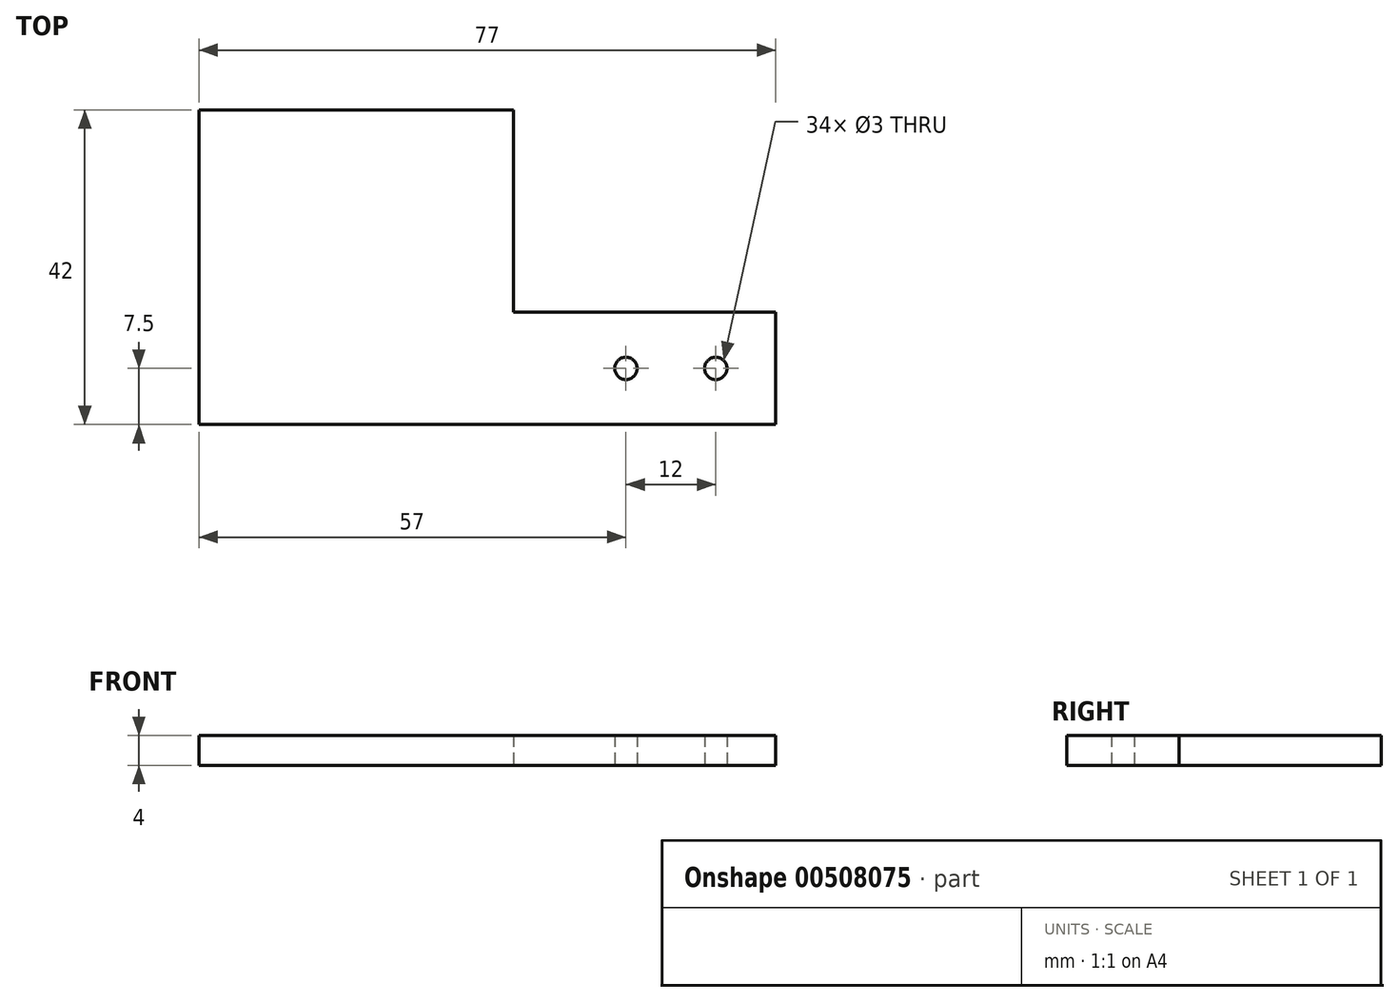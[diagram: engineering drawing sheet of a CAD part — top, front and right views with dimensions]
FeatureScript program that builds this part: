
annotation { "Feature Type Name" : "Feature", "Feature Type Description" : "" }
export const myFeature = defineFeature(function(context is Context, id is Id, definition is map)
    precondition{}
    {
        {
            var Q0;
            Q0=qCreatedBy(makeId("Top.planeOp"),FACE);
            var sketch = newSketch(context, id + "F0", { "sketchPlane" : qUnion([Q0])});
            skLineSegment(sketch, "E0.bottom", {"start": v(-21, 21) * mm, "end": v(21, 21) * mm});
            skLineSegment(sketch, "E0.top", {"start": v(-21, -21) * mm, "end": v(21, -21) * mm});
            skLineSegment(sketch, "E0.left", {"start": v(-21, 21) * mm, "end": v(-21, -21) * mm});
            skLineSegment(sketch, "E0.right", {"start": v(21, 21) * mm, "end": v(21, -6) * mm});
            skPoint(sketch, "E0.middle", {"position": v(0, 0) * mm});
            skLineSegment(sketch, "E1", {"start": v(21, -21) * mm, "end": v(56, -21) * mm});
            skLineSegment(sketch, "E2", {"start": v(56, -21) * mm, "end": v(56, -6) * mm});
            skLineSegment(sketch, "E3", {"start": v(56, -6) * mm, "end": v(21, -6) * mm});
            skPoint(sketch, "E3.endSnap0", {"position": v(21, 0) * mm});
            skLineSegment(sketch, "E4", {"start": v(56, -13.5) * mm, "end": v(48, -13.5) * mm, "construction": true});
            skCircle(sketch, "E5", {"center": v(48, -13.5) * mm, "radius": 1.5 * mm});
            skLineSegment(sketch, "E6", {"start": v(48, -13.5) * mm, "end": v(36, -13.5) * mm, "construction": true});
            skCircle(sketch, "E7", {"center": v(36, -13.5) * mm, "radius": 1.5 * mm});
            skSolve(sketch);
        }
        {
            var Q0;
            Q0 = qSketchRegion(id + "F0", true);
            extrude(context, id + "F1", {"entities" : qUnion([Q0]), "depth" : 4 * mm});
        }
    });
